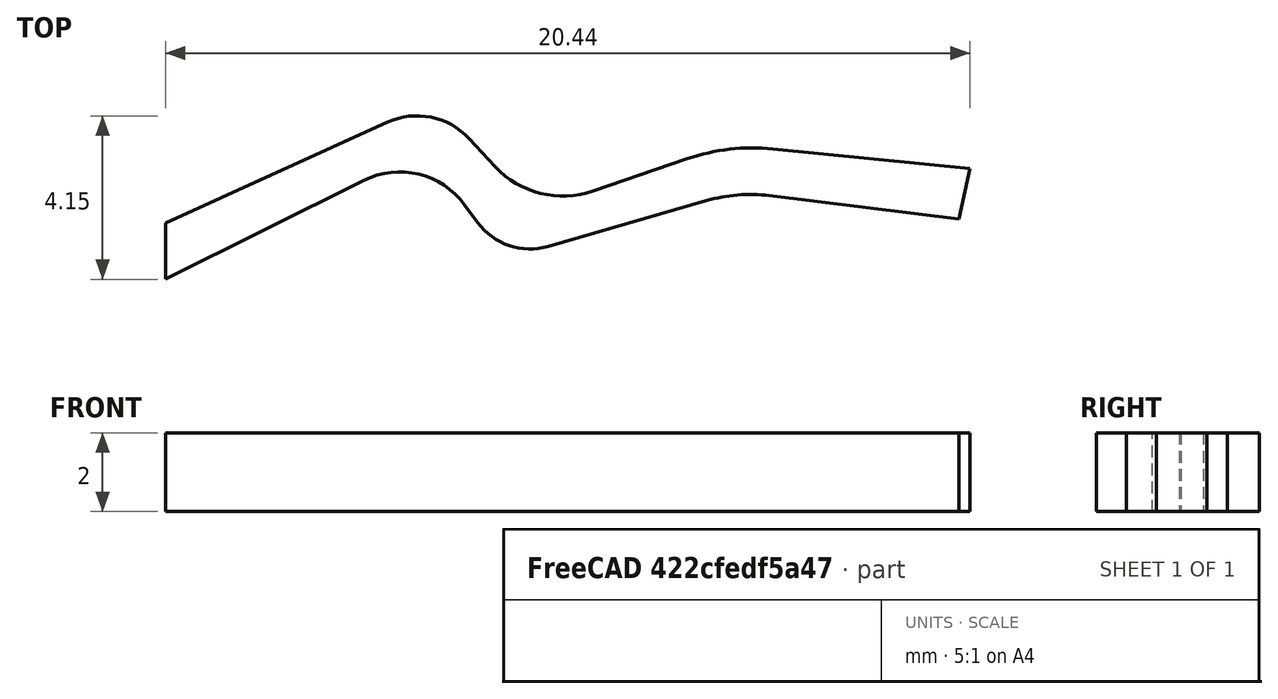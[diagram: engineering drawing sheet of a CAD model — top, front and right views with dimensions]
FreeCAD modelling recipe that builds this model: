
FCSTD DOCUMENT  (FreeCAD 0.14R3702 (Git))
Label: guirlande15
License: CC-BY 3.0
LicenseURL: http://creativecommons.org/licenses/by/3.0/
objects: Sketcher::SketchObject×1, PartDesign::Pad×1
note: 3 computed .brp shape members not serialized (recipe doc carries the construction recipe); baked Part::Feature solids carry a one-line shape summary decoded from their .brp

FEATURE [Sketcher::SketchObject] Sketch
  sketch-geometry (16):
    g0: LineSegment StartX=-60.1056 StartY=45.5336 StartZ=0 EndX=-54.4666 EndY=48.0918 EndZ=0
    g1: LineSegment StartX=-52.4033 StartY=47.6786 StartZ=0 EndX=-51.738 EndY=46.9639 EndZ=0
    g2: LineSegment StartX=-49.2477 StartY=46.3403 StartZ=0 EndX=-46.847 EndY=47.1636 EndZ=0
    g3: LineSegment StartX=-44.6794 StartY=47.4147 StartZ=0 EndX=-39.6748 EndY=46.9137 EndZ=0
    g4: LineSegment StartX=-39.6748 StartY=46.9137 StartZ=0 EndX=-39.9529 EndY=45.6345 EndZ=0
    g5: LineSegment StartX=-39.9529 StartY=45.6345 StartZ=0 EndX=-44.7741 EndY=46.226 EndZ=0
    g6: LineSegment StartX=-46.3723 StartY=46.098 StartZ=0 EndX=-50.3902 EndY=44.9344 EndZ=0
    g7: LineSegment StartX=-52.1803 StartY=45.5425 StartZ=0 EndX=-52.5105 EndY=45.9917 EndZ=0
    g8: LineSegment StartX=-55.0744 StartY=46.6116 StartZ=0 EndX=-60.1056 EndY=44.1035 EndZ=0
    g9: LineSegment StartX=-60.1056 StartY=44.1035 StartZ=0 EndX=-60.1056 EndY=45.5336 EndZ=0
    g10: ArcOfCircle CenterX=-53.7222 CenterY=46.4509 CenterZ=0 NormalX=0 NormalY=0 NormalZ=1 Radius=1.80189 StartAngle=0.749638 EndAngle=1.99668
    g11: ArcOfCircle CenterX=-54.1607 CenterY=44.7787 CenterZ=0 NormalX=0 NormalY=0 NormalZ=1 Radius=2.04805 StartAngle=0.633899 EndAngle=2.03324
    g12: ArcOfCircle CenterX=-50.8497 CenterY=46.5207 CenterZ=0 NormalX=0 NormalY=0 NormalZ=1 Radius=1.65149 StartAngle=3.77549 EndAngle=4.99429
    g13: ArcOfCircle CenterX=-50.0125 CenterY=48.5703 CenterZ=0 NormalX=0 NormalY=0 NormalZ=1 Radius=2.35749 StartAngle=3.89123 EndAngle=5.04278
    g14: ArcOfCircle CenterX=-45.2607 CenterY=42.2599 CenterZ=0 NormalX=0 NormalY=0 NormalZ=1 Radius=3.99592 StartAngle=1.44872 EndAngle=1.8527
    g15: ArcOfCircle CenterX=-45.1886 CenterY=42.3281 CenterZ=0 NormalX=0 NormalY=0 NormalZ=1 Radius=5.11202 StartAngle=1.47103 EndAngle=1.90118
  constraints (17):
    c: Coincident(g3,g4)
    c: Coincident(g4,g5)
    c: Coincident(g8,g9)
    c: Coincident(g9,g0)
    c: Vertical(g9)
    c: Tangent(g1,g10)
    c: Tangent(g0,g10)
    c: Tangent(g8,g11)
    c: Tangent(g7,g11)
    c: Tangent(g7,g12)
    c: Tangent(g6,g12)
    c: Tangent(g1,g13)
    c: Tangent(g2,g13)
    c: Tangent(g6,g14)
    c: Tangent(g5,g14)
    c: Tangent(g2,g15)
    c: Tangent(g3,g15)
FEATURE [PartDesign::Pad] Pad
  Length = 2
  Length2 = 100
  Sketch = -> Sketch
  Type = 0
